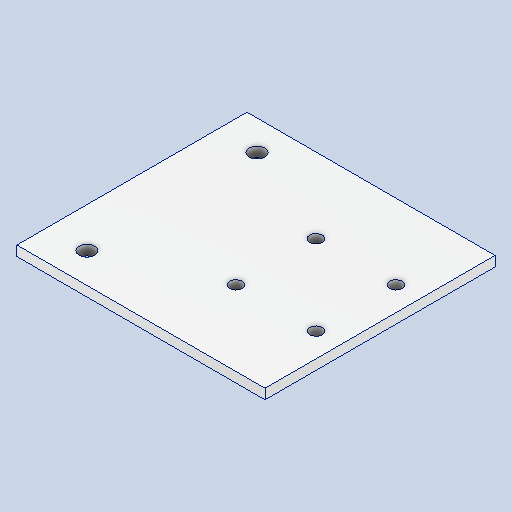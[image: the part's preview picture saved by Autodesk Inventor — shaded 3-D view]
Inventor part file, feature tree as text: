
AUTODESK INVENTOR PART (.ipt)
format: ipt  version: 2023 (Build 270158000, 158)  size: 109,056 bytes
history: native  units: in
note: dims shown in document units (in); Inventor stores cm internally (conversion verified against a paired STEP export)
features: other x3, sketch x2
ambient origin geometry x8: Origin, YZ Plane, XZ Plane, XY Plane, X Axis, Y Axis, Z Axis, Center Point
bodies: Solid1 (feature_tree)
feature tree (5):
  other  "MotorMount.ipt"
  other  "Solid1::MotorMount.ipt"
  other  "TaggingFeature1"
  sketch  "Sketch1"  dims[d0=0.3937in]
  sketch  "Sketch2"
